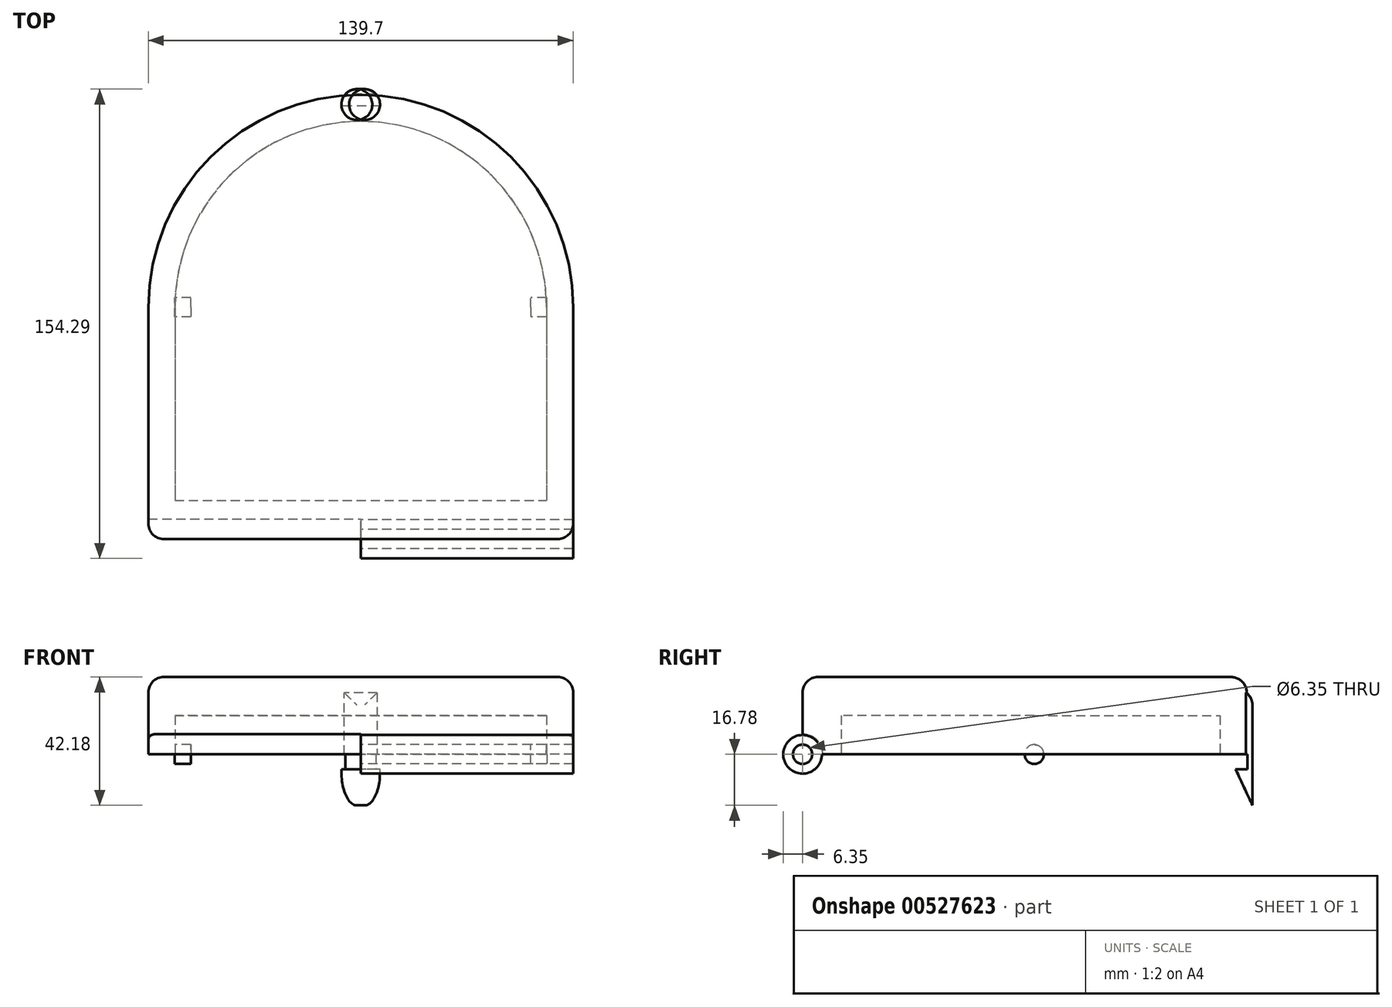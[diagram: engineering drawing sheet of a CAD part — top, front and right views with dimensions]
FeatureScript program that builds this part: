
annotation { "Feature Type Name" : "Feature", "Feature Type Description" : "" }
export const myFeature = defineFeature(function(context is Context, id is Id, definition is map)
    precondition{}
    {
        {
            var Q0;
            Q0=qCreatedBy(makeId("Top.planeOp"),FACE);
            var sketch = newSketch(context, id + "F0", { "sketchPlane" : qUnion([Q0])});
            skArc(sketch, "E0", {"start": v(69.85, 0) * mm, "mid": v(0, 69.85) * mm, "end": v(-69.85, 0) * mm});
            skLineSegment(sketch, "E1", {"start": v(-69.85, 0) * mm, "end": v(-69.85, -76.2) * mm});
            skLineSegment(sketch, "E2", {"start": v(69.85, 0) * mm, "end": v(69.85, -76.2) * mm});
            skLineSegment(sketch, "E3", {"start": v(-69.85, -76.2) * mm, "end": v(69.85, -76.2) * mm});
            skSolve(sketch);
        }
        {
            var Q0;
            Q0=qCreatedBy(makeId("Top.planeOp"),FACE);
            var sketch = newSketch(context, id + "F1", { "sketchPlane" : qUnion([Q0])});
            skArc(sketch, "E4", {"start": v(61.12, 0) * mm, "mid": v(0, 61.12) * mm, "end": v(-61.12, 0) * mm});
            skLineSegment(sketch, "E5", {"start": v(-61.12, 0) * mm, "end": v(-61.12, -63.5) * mm});
            skLineSegment(sketch, "E6", {"start": v(61.12, 0) * mm, "end": v(61.12, -63.5) * mm});
            skLineSegment(sketch, "E7", {"start": v(-61.12, -63.5) * mm, "end": v(61.12, -63.5) * mm});
            skSolve(sketch);
        }
        {
            var Q0;
            Q0=qCreatedBy(makeId("Right.planeOp"),FACE);
            var sketch = newSketch(context, id + "F2", { "sketchPlane" : qUnion([Q0])});
            skCircle(sketch, "E8", {"center": v(-76.2, 0) * mm, "radius": 6.67 * mm});
            skSolve(sketch);
        }
        {
            var Q0;
            Q0=qCreatedBy(makeId("Right.planeOp"),FACE);
            var sketch = newSketch(context, id + "F3", { "sketchPlane" : qUnion([Q0])});
            skCircle(sketch, "E9", {"center": v(-76.2, 0) * mm, "radius": 6.35 * mm});
            skSolve(sketch);
        }
        {
            var Q0;
            Q0 = qSketchRegion(id + "F0", true);
            extrude(context, id + "F4", {"entities" : qUnion([Q0]), "depth" : 25.4 * mm, "offsetDistance" : 25.4 * mm});
        }
        {
            var Q0;
            Q0 = qSketchRegion(id + "F1", true);
            extrude(context, id + "F5", {"entities" : qUnion([Q0]), "operationType" : NewBodyOperationType.REMOVE, "depth" : 12.7 * mm, "offsetDistance" : 25.4 * mm});
        }
        {
            var Q0;
            Q0 = qSketchRegion(id + "F2", true);
            extrude(context, id + "F6", {"entities" : qUnion([Q0]), "operationType" : NewBodyOperationType.REMOVE, "oppositeDirection" : true, "depth" : 69.85 * mm, "offsetDistance" : 25.4 * mm});
        }
        {
            var Q0;
            Q0 = qSketchRegion(id + "F3", true);
            extrude(context, id + "F7", {"entities" : qUnion([Q0]), "operationType" : NewBodyOperationType.ADD, "depth" : 69.85 * mm, "offsetDistance" : 25.4 * mm});
        }
        {
            var Q0;
            Q0=makeQuery(id+"F4.opExtrude","CAP_EDGE",EDGE,{"disambiguationData":[OSD([sQuery(id+"F0.wireOp",EDGE,"E1")])],"isStart":false});
            fillet(context, id + "F8", {"entities" : qUnion([Q0]), "radius" : 5.08 * mm, "tangentPropagation" : true, "allowEdgeOverflow" : false});
        }
        {
            var Q0;
            Q0=makeQuery(id+"F4.opExtrude","CAP_EDGE",EDGE,{"disambiguationData":[OSD([sQuery(id+"F0.wireOp",EDGE,"E3")])],"isStart":false});
            fillet(context, id + "F9", {"entities" : qUnion([Q0]), "radius" : 5.08 * mm, "tangentPropagation" : true, "allowEdgeOverflow" : false});
        }
        {
            var Q0;
            Q0=sQuery(id+"F2.wireOp",VERTEX,"E8.center");
            var Q1;
            Q1=makeQuery(id+"F4.opExtrude","SWEPT_BODY",BODY,{"disambiguationData":[OSD([sQuery(id+"F0.wireOp",EDGE,"E0"),sQuery(id+"F0.wireOp",EDGE,"E1"),sQuery(id+"F0.wireOp",EDGE,"E2"),sQuery(id+"F0.wireOp",EDGE,"E3")])]});
            hole(context, id + "F10", {"style" : HoleStyle.SIMPLE, "endStyle" : HoleEndStyle.THROUGH, "oppositeDirection" : true, "holeDiameter" : 6.35 * mm, "isTappedThrough" : true, "tappedDepth" : 12.7 * mm, "tapClearance" : 3, "locations" : qUnion([Q0]), "scope" : qUnion([Q1])});
        }
        {
            var Q0;
            Q0=qCreatedBy(makeId("Right.planeOp"),FACE);
            var sketch = newSketch(context, id + "F11", { "sketchPlane" : qUnion([Q0])});
            skLineSegment(sketch, "E10", {"start": v(65.3, 20.19) * mm, "end": v(71.74, 20.19) * mm});
            skLineSegment(sketch, "E11", {"start": v(71.74, 20.19) * mm, "end": v(71.74, -16.78) * mm});
            skLineSegment(sketch, "E12", {"start": v(71.74, -16.78) * mm, "end": v(66.18, -4.86) * mm});
            skLineSegment(sketch, "E13", {"start": v(66.18, -4.86) * mm, "end": v(70.1, -4.86) * mm});
            skLineSegment(sketch, "E14", {"start": v(70.1, -4.86) * mm, "end": v(70.1, 0) * mm});
            skLineSegment(sketch, "E15", {"start": v(70.1, 0) * mm, "end": v(65.36, 0) * mm});
            skLineSegment(sketch, "E16", {"start": v(65.36, 0) * mm, "end": v(65.3, 20.19) * mm});
            skSolve(sketch);
        }
        {
            var Q0;
            Q0 = qSketchRegion(id + "F11", true);
            extrude(context, id + "F12", {"entities" : qUnion([Q0]), "operationType" : NewBodyOperationType.ADD, "depth" : 6.35 * mm, "offsetDistance" : 25.4 * mm, "hasSecondDirection" : true, "secondDirectionOppositeDirection" : true, "secondDirectionDepth" : 6.35 * mm});
        }
        {
            var Q0;
            Q0=makeQuery(id+"F12.opExtrude","CAP_EDGE",EDGE,{"disambiguationData":[OSD([sQuery(id+"F11.wireOp",EDGE,"E11")])],"isStart":false});
            fillet(context, id + "F13", {"entities" : qUnion([Q0]), "radius" : 5.08 * mm, "tangentPropagation" : true, "allowEdgeOverflow" : false});
        }
        {
            var Q0;
            Q0=makeQuery(id+"F12.opExtrude","CAP_EDGE",EDGE,{"disambiguationData":[OSD([sQuery(id+"F11.wireOp",EDGE,"E11")])],"isStart":true});
            fillet(context, id + "F14", {"entities" : qUnion([Q0]), "radius" : 5.08 * mm, "tangentPropagation" : true, "allowEdgeOverflow" : false});
        }
        {
            var Q0;
            Q0=makeQuery(id+"F12.opExtrude","SWEPT_EDGE",EDGE,{"disambiguationData":[OSD([sQuery(id+"F11.wireOp",EDGE,"E10"),sQuery(id+"F11.wireOp",EDGE,"E11")])]});
            fillet(context, id + "F15", {"entities" : qUnion([Q0]), "radius" : 5.08 * mm, "tangentPropagation" : true, "allowEdgeOverflow" : false});
        }
        {
            var Q0;
            Q0=qCreatedBy(makeId("Right.planeOp"),FACE);
            var sketch = newSketch(context, id + "F16", { "sketchPlane" : qUnion([Q0])});
            skCircle(sketch, "E17", {"center": v(0, 0) * mm, "radius": 3.18 * mm});
            skSolve(sketch);
        }
        {
            var Q0;
            Q0 = qSketchRegion(id + "F16", true);
            extrude(context, id + "F17", {"entities" : qUnion([Q0]), "operationType" : NewBodyOperationType.ADD, "depth" : 61.2 * mm, "offsetDistance" : 25.4 * mm, "hasSecondDirection" : true, "secondDirectionOppositeDirection" : true, "secondDirectionDepth" : 61.2 * mm});
        }
        {
            var Q0;
            Q0=qCreatedBy(makeId("Right.planeOp"),FACE);
            var sketch = newSketch(context, id + "F18", { "sketchPlane" : qUnion([Q0])});
            skCircle(sketch, "E18", {"center": v(0, 0) * mm, "radius": 3.18 * mm});
            skSolve(sketch);
        }
        {
            var Q0;
            Q0 = qSketchRegion(id + "F18", true);
            extrude(context, id + "F19", {"entities" : qUnion([Q0]), "operationType" : NewBodyOperationType.REMOVE, "oppositeDirection" : true, "depth" : 55.88 * mm, "offsetDistance" : 25.4 * mm, "hasSecondDirection" : true, "secondDirectionOppositeDirection" : false, "secondDirectionDepth" : 55.88 * mm});
        }
    });
